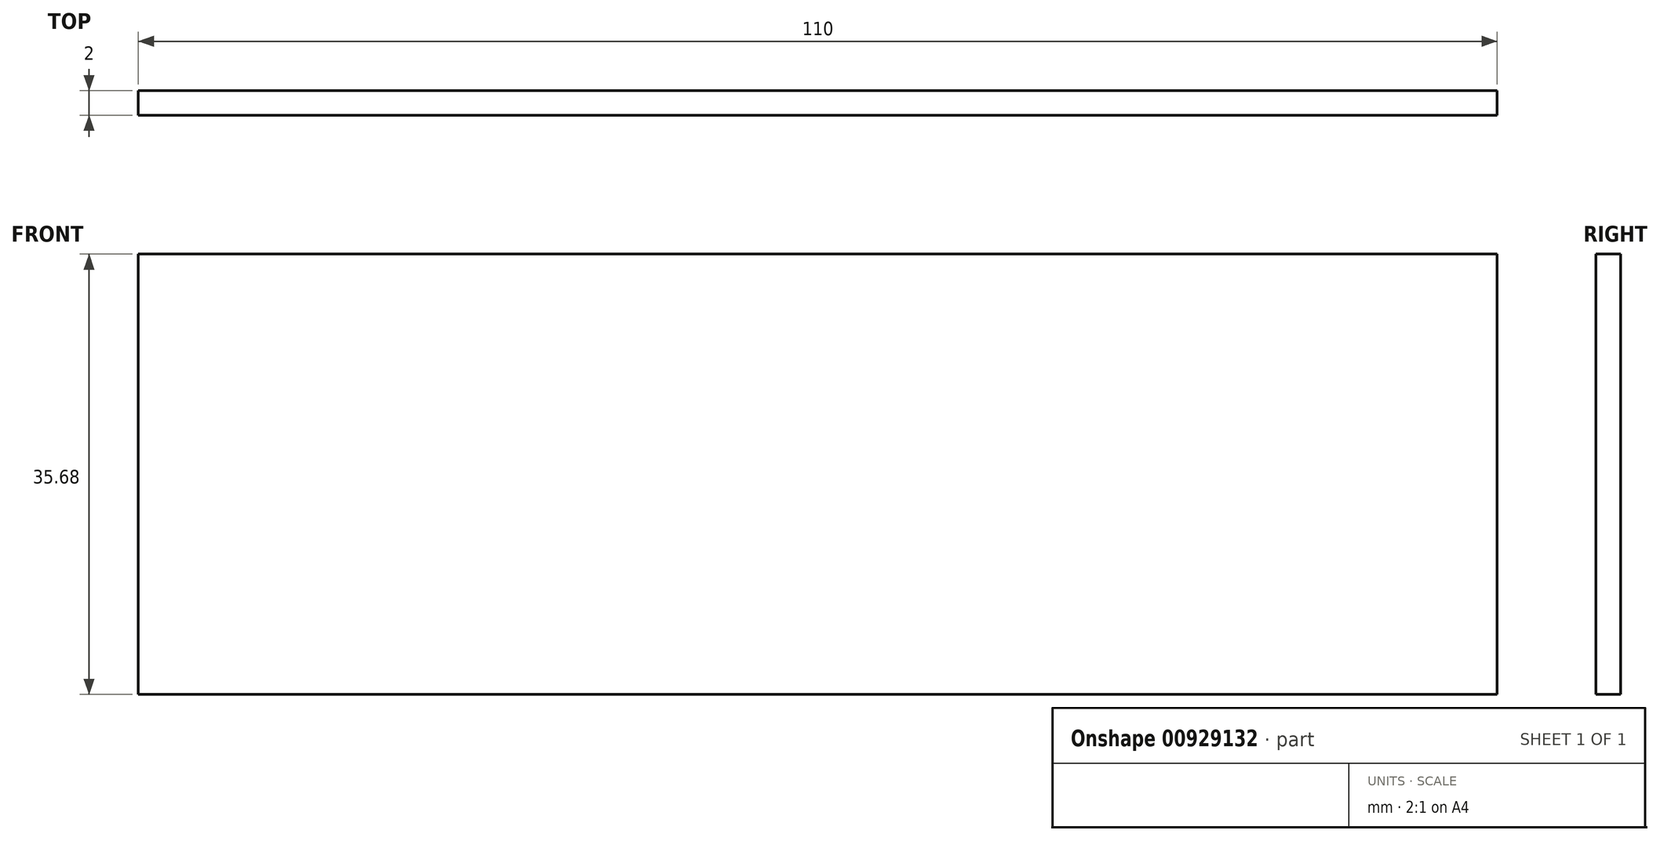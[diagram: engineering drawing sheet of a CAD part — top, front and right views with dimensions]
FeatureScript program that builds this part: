
annotation { "Feature Type Name" : "Feature", "Feature Type Description" : "" }
export const myFeature = defineFeature(function(context is Context, id is Id, definition is map)
    precondition{}
    {
        {
            var Q0;
            Q0=qCreatedBy(makeId("Front.planeOp"),FACE);
            var sketch = newSketch(context, id + "F0", { "sketchPlane" : qUnion([Q0])});
            skLineSegment(sketch, "E0.bottom", {"start": v(-55, 17.84) * mm, "end": v(55, 17.84) * mm});
            skLineSegment(sketch, "E0.top", {"start": v(-55, -17.84) * mm, "end": v(55, -17.84) * mm});
            skLineSegment(sketch, "E0.left", {"start": v(-55, 17.84) * mm, "end": v(-55, -17.84) * mm});
            skLineSegment(sketch, "E0.right", {"start": v(55, 17.84) * mm, "end": v(55, -17.84) * mm});
            skPoint(sketch, "E0.middle", {"position": v(0, 0) * mm});
            skSolve(sketch);
        }
        {
            var Q0;
            Q0 = qSketchRegion(id + "F0", true);
            extrude(context, id + "F1", {"entities" : qUnion([Q0]), "depth" : 2 * mm, "hasOffset" : true, "offsetDistance" : 2 * mm});
        }
    });
